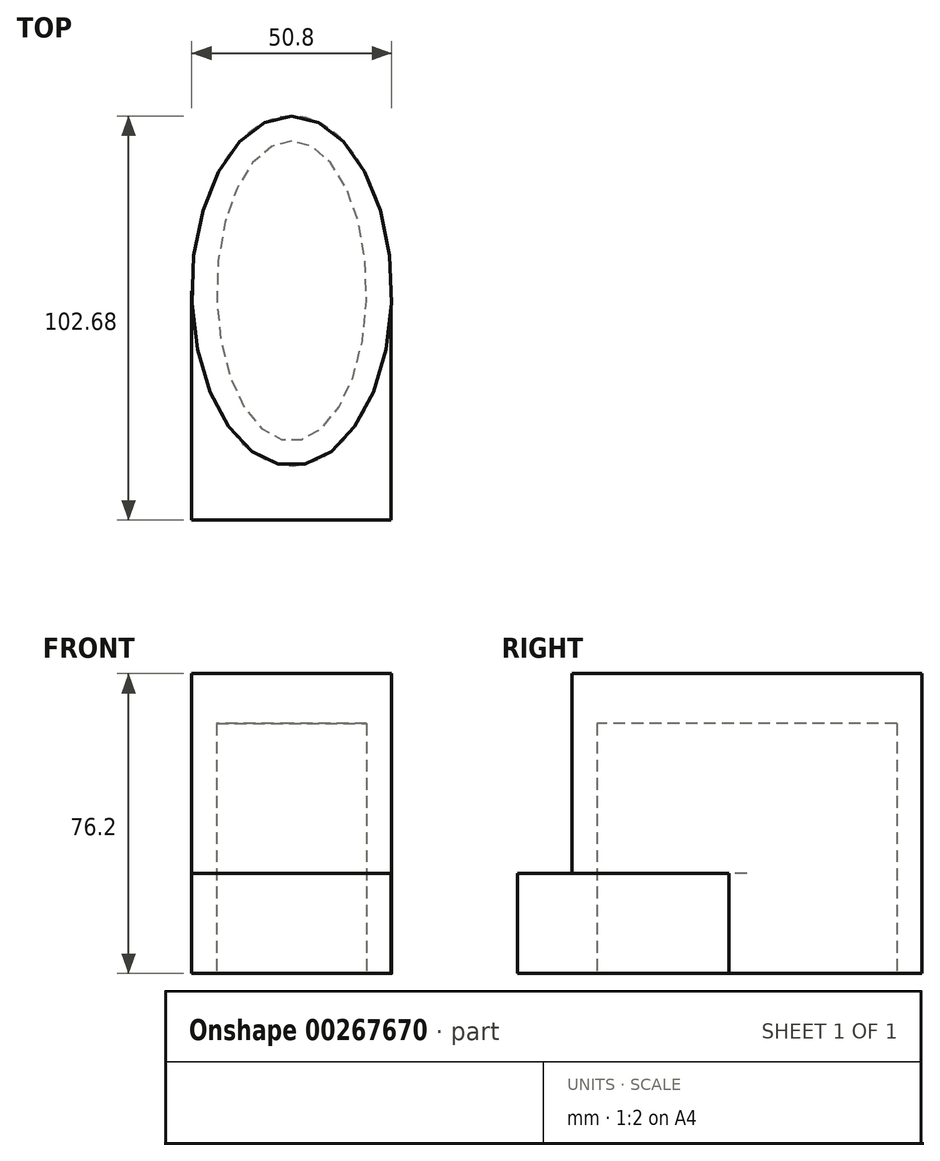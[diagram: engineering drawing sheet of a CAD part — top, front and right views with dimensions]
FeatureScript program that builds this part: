
annotation { "Feature Type Name" : "Feature", "Feature Type Description" : "" }
export const myFeature = defineFeature(function(context is Context, id is Id, definition is map)
    precondition{}
    {
        {
            var Q0;
            Q0=qCreatedBy(makeId("Top.planeOp"),FACE);
            var sketch = newSketch(context, id + "F0", { "sketchPlane" : qUnion([Q0])});
            skEllipse(sketch, "E0", {"center": v(0, 0) * mm, "majorRadius": 44.45 * mm, "minorRadius": 25.4 * mm, "majorAxis": v(0, 1)});
            skEllipse(sketch, "E1", {"center": v(0, 0) * mm, "majorRadius": 38.1 * mm, "minorRadius": 19.05 * mm, "majorAxis": v(0, 1)});
            skPoint(sketch, "E2", {"position": v(0, 44.45) * mm});
            skLineSegment(sketch, "E3.bottom", {"start": v(-25.4, 0) * mm, "end": v(25.27, 0) * mm});
            skLineSegment(sketch, "E3.top", {"start": v(-25.4, -58.23) * mm, "end": v(25.27, -58.23) * mm});
            skLineSegment(sketch, "E3.left", {"start": v(-25.4, 0) * mm, "end": v(-25.4, -58.23) * mm});
            skLineSegment(sketch, "E3.right", {"start": v(25.27, 0) * mm, "end": v(25.27, -58.23) * mm});
            skSolve(sketch);
        }
        {
            var Q0;
            Q0=makeQuery(id+"F0.imprint","IMPRINT",FACE,{"disambiguationData":[TD([[makeQuery(id+"F0.imprint","IMPRINT",EDGE,{"derivedFrom":sQuery(id+"F0.wireOp",EDGE,"E1")}),1.0]])]});
            var Q1;
            Q1=makeQuery(id+"F0.imprint","IMPRINT",FACE,{"disambiguationData":[TD([[makeQuery(id+"F0.imprint","IMPRINT",EDGE,{"derivedFrom":sQuery(id+"F0.wireOp",EDGE,"E0")}),1.0]])]});
            extrude(context, id + "F1", {"entities" : qUnion([Q0, Q1]), "depth" : 76.2 * mm});
        }
        {
            var Q0;
            Q0=makeQuery(id+"F0.imprint","IMPRINT",FACE,{"disambiguationData":[TD([[makeQuery(id+"F0.imprint","IMPRINT",EDGE,{"derivedFrom":sQuery(id+"F0.wireOp",EDGE,"E1")}),1.0]])]});
            extrude(context, id + "F2", {"entities" : qUnion([Q0]), "operationType" : NewBodyOperationType.REMOVE, "depth" : 63.5 * mm});
        }
        {
            var Q0;
            Q0 = qSketchRegion(id + "F0", true);
            extrude(context, id + "F3", {"entities" : qUnion([Q0]), "operationType" : NewBodyOperationType.ADD, "depth" : 25.4 * mm});
        }
    });
